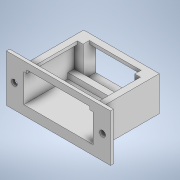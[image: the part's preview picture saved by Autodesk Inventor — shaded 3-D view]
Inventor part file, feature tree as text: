
AUTODESK INVENTOR PART (.ipt)
format: ipt  version: 2020 (Build 240168000, 168)  size: 368,640 bytes
history: native  units: in
note: dims shown in document units (in); Inventor stores cm internally (conversion verified against a paired STEP export)
features: extrude x7, sketch x4
ambient origin geometry x8: Origin, YZ Plane, XZ Plane, XY Plane, X Axis, Y Axis, Z Axis, Center Point
bodies: Solid1 (feature_tree)
feature tree (11):
  extrude  "Extrusion1"  Depth=0.75in
  extrude  "Extrusion2"  Depth=0.094in
  extrude  "Extrusion3"  Depth=0.125in
  extrude  "Extrusion4"  Depth=0.2in
  extrude  "Extrusion6"  Depth=0.05in TaperAngle=0.0deg
  extrude  "Extrusion7"  Depth=1.0in TaperAngle=0.0deg
  extrude  "Extrusion8"  Depth=1.0in TaperAngle=0.0deg
  sketch  "Sketch1"  dims[d0=1.65in d1=0.75in]
  sketch  "Sketch2"  dims[d2=0.094in d3=0.094in]
  sketch  "Sketch3"  dims[d4=0.125in d5=0.125in]
  sketch  "Sketch4"  dims[d6=0.375in d7=0.375in d8=0.05in d9=0.0in d12=1.0in d13=0.0in d18=1.0in d19=0.0in d21=0.9in d22=0.0in d31=0.55in d32=0.1in d33=1.2in d34=0.225in d35=0.05in d36=0.05in d37=0.05in d38=0.05in d39=0.05in d40=0.05in d44=0.09in d45=0.0in d46=0.14in d47=0.2in d48=0.14in d49=0.2in d50=0.5in d51=0.0in d52=0.01in d53=0.0in d54=0.1in d55=0.2in]
